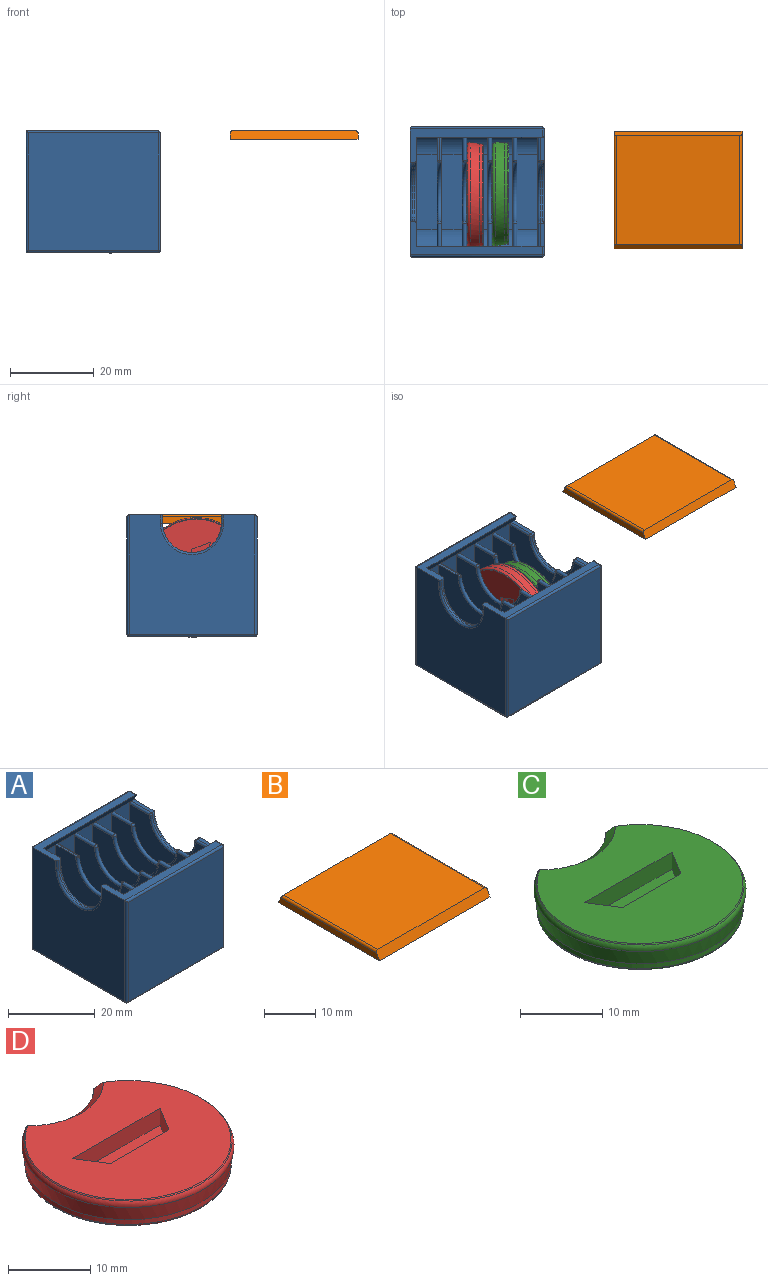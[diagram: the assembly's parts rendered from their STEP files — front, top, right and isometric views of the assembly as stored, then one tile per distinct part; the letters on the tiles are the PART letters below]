
ASSEMBLY  parts=4 mates=3
PART A: 104 faces, bbox 32x31x29 mm
  f0: plane 6.52x0.5mm, normal (0,0,1), area 3.3mm2, adj f13,f52,f53,f59,f84
  f1: plane 6.52x1mm, normal (0,0,1), area 6.5mm2, adj f2,f45,f46,f57,f74
  f2: plane 30x28mm, normal (1,0,0), area 710.8mm2, adj f1,f26,f45,f57,f59,f86,f89,f94
  f3: plane 30x28.5mm, normal (-1,0,0), area 736.6mm2, adj f55,f56,f58,f60,f65,f90,f95,f101
  f4: plane 28x25.5mm, normal (-1,0,0), area 622.4mm2, adj f5,f25,f32,f41,f42,f48,f74,f78
  f5: plane 21x6mm, normal (0,1,0), area 105.1mm2, adj f4,f6,f42,f57,f72,f74
  f6: plane 28x25.5mm, normal (1,0,0), area 622.4mm2, adj f5,f25,f32,f41,f42,f49,f72,f76
  f7: plane 28x25.5mm, normal (-1,0,0), area 622.4mm2, adj f8,f21,f30,f37,f38,f50,f70,f82
  f8: plane 21x6mm, normal (0,1,0), area 105.1mm2, adj f7,f9,f38,f57,f68,f70
  f9: plane 28x25.5mm, normal (1,0,0), area 622.4mm2, adj f8,f21,f30,f37,f38,f51,f68,f80
  f10: plane 28x25.5mm, normal (-1,0,0), area 622.4mm2, adj f11,f22,f29,f35,f36,f51,f68,f80
  f11: plane 21x6mm, normal (0,1,0), area 105.1mm2, adj f10,f12,f36,f57,f66,f68
  f12: plane 28x25.5mm, normal (1,0,0), area 622.4mm2, adj f11,f22,f29,f35,f36,f52,f66,f84
  f13: plane 28x26mm, normal (-1,0,0), area 625.7mm2, adj f0,f14,f23,f28,f33,f34,f52,f66
  f14: plane 21x5.5mm, normal (0,1,0), area 105.1mm2, adj f13,f15,f34,f57,f66
  f15: plane 28x28mm, normal (1,0,0), area 652.9mm2, adj f14,f23,f28,f33,f34,f54,f56,f57
  f16: plane 31x28mm, normal (0,-1,0), area 868mm2, adj f88,f89,f90,f91
  f17: plane 31x28mm, normal (0,1,0), area 868mm2, adj f96,f99,f101,f103
  f18: plane 21x6mm, normal (0,1,0), area 105.1mm2, adj f19,f24,f39,f57,f70,f72
  f19: plane 28x25.5mm, normal (1,0,0), area 622.4mm2, adj f18,f20,f31,f39,f40,f50,f70,f82
  f20: plane 21x6mm, normal (0,-1,0), area 105.1mm2, adj f19,f24,f40,f59,f76,f82
  f21: plane 21x6mm, normal (0,-1,0), area 105.1mm2, adj f7,f9,f37,f59,f80,f82
  f22: plane 21x6mm, normal (0,-1,0), area 105.1mm2, adj f10,f12,f35,f59,f80,f84
  f23: plane 21x5mm, normal (0,-1,0), area 105mm2, adj f13,f15,f33,f59
  f24: plane 28x25.5mm, normal (-1,0,0), area 622.4mm2, adj f18,f20,f31,f39,f40,f49,f72,f76
  f25: plane 21x6mm, normal (0,-1,0), area 105.1mm2, adj f4,f6,f41,f59,f76,f78
  f26: plane 6.52x1mm, normal (0,0,1), area 6.5mm2, adj f2,f45,f47,f59,f78
  f27: plane 31x30mm, normal (0,0,-1), area 930mm2, adj f91,f94,f95,f96
  f28: plane 18x5mm, normal (0,0,1), area 90mm2, adj f13,f15,f33,f34
  f29: plane 18x5mm, normal (0,0,1), area 90mm2, adj f10,f12,f35,f36
  f30: plane 18x5mm, normal (0,0,1), area 90mm2, adj f7,f9,f37,f38
  f31: plane 18x5mm, normal (0,0,1), area 90mm2, adj f19,f24,f39,f40
  f32: plane 18x5mm, normal (0,0,1), area 90mm2, adj f4,f6,f41,f42
  f33: cylinder r=5mm len=5mm, axis (1,0,0), area 39.3mm2, adj f13,f15,f23,f28
  f34: cylinder r=5mm len=5mm, axis (-1,0,0), area 39.3mm2, adj f13,f14,f15,f28
  f35: cylinder r=5mm len=5mm, axis (1,0,0), area 39.3mm2, adj f10,f12,f22,f29
  f36: cylinder r=5mm len=5mm, axis (-1,0,0), area 39.3mm2, adj f10,f11,f12,f29
  f37: cylinder r=5mm len=5mm, axis (1,0,0), area 39.3mm2, adj f7,f9,f21,f30
  f38: cylinder r=5mm len=5mm, axis (-1,0,0), area 39.3mm2, adj f7,f8,f9,f30
  f39: cylinder r=5mm len=5mm, axis (-1,0,0), area 39.3mm2, adj f18,f19,f24,f31
  f40: cylinder r=5mm len=5mm, axis (1,0,0), area 39.3mm2, adj f19,f20,f24,f31
  f41: cylinder r=5mm len=5mm, axis (1,0,0), area 39.3mm2, adj f4,f6,f25,f32
  f42: cylinder r=5mm len=5mm, axis (-1,0,0), area 39.3mm2, adj f4,f5,f6,f32
  f43: cylinder r=7mm len=14mm, axis (-1,0,0), area 11mm2, adj f54,f55,f61,f64
  f44: cylinder r=7mm len=13.97mm, axis (-1,0,0), area 10.5mm2, adj f45,f46,f47,f48
  f45: torus R=7.5mm, axis (1,0,0), area 17.5mm2, adj f1,f2,f26,f44,f46,f47
  f46: cylinder r=0.5mm len=1mm, axis (-1,0,0), area 0.6mm2, adj f1,f44,f45,f75
  f47: cylinder r=0.5mm len=1mm, axis (-1,0,0), area 0.6mm2, adj f26,f44,f45,f79
  f48: torus R=7.5mm, axis (1,0,0), area 17mm2, adj f4,f44,f75,f79
  f49: torus R=7.5mm, axis (1,0,0), area 33.9mm2, adj f6,f24,f73,f77
  f50: torus R=7.5mm, axis (1,0,0), area 33.9mm2, adj f7,f19,f71,f83
  f51: torus R=7.5mm, axis (1,0,0), area 33.9mm2, adj f9,f10,f69,f81
  f52: torus R=7.5mm, axis (1,0,0), area 34.2mm2, adj f0,f12,f13,f53,f67,f85
  f53: cylinder r=0.5mm len=0.5mm, axis (-1,0,0), area 0.2mm2, adj f0,f52,f85
  f54: torus R=7.5mm, axis (1,0,0), area 17.7mm2, adj f15,f43,f62,f63
  f55: torus R=7.5mm, axis (1,0,0), area 17.7mm2, adj f3,f43,f60,f65
  f56: plane 31.5x8mm, normal (0,0,1), area 71.9mm2, adj f3,f15,f57,f63,f64,f65,f86,f88
  f57: plane 30.5x2mm, normal (0,0.89,-0.45), area 68.1mm2, adj f1,f2,f5,f8,f11,f14,f15,f18
  f58: plane 31.5x8mm, normal (0,0,1), area 71.9mm2, adj f3,f15,f59,f60,f61,f62,f100,f103
  f59: plane 30.5x2mm, normal (0,-0.89,-0.45), area 68.1mm2, adj f0,f2,f15,f20,f21,f22,f23,f25
  f60: cylinder r=0.5mm len=2mm, axis (0,0,-1), area 1.6mm2, adj f3,f55,f58,f61
  f61: plane 2x0.5mm, normal (0,-1,0), area 1mm2, adj f43,f58,f60,f62
  f62: cylinder r=0.5mm len=2mm, axis (0,0,-1), area 1.6mm2, adj f15,f54,f58,f61
  f63: cylinder r=0.5mm len=2mm, axis (0,0,-1), area 1.6mm2, adj f15,f54,f56,f64
  f64: plane 2x0.5mm, normal (0,1,0), area 1mm2, adj f43,f56,f63,f65
  f65: cylinder r=0.5mm len=2mm, axis (0,0,-1), area 1.6mm2, adj f3,f55,f56,f64
  f66: cylinder r=0.5mm len=6.52mm, axis (0,-1,0), area 10.2mm2, adj f11,f12,f13,f14,f67
  f67: sphere r=0.5mm, area 0.8mm2, adj f52,f66
  f68: cylinder r=0.5mm len=6.52mm, axis (0,-1,0), area 10.2mm2, adj f8,f9,f10,f11,f69
  f69: sphere r=0.5mm, area 0.8mm2, adj f51,f68
  f70: cylinder r=0.5mm len=6.52mm, axis (0,-1,0), area 10.2mm2, adj f7,f8,f18,f19,f71
  f71: sphere r=0.5mm, area 0.8mm2, adj f50,f70
  f72: cylinder r=0.5mm len=6.52mm, axis (0,-1,0), area 10.2mm2, adj f5,f6,f18,f24,f73
  f73: sphere r=0.5mm, area 0.8mm2, adj f49,f72
  f74: cylinder r=0.5mm len=6.52mm, axis (0,1,0), area 5.1mm2, adj f1,f4,f5,f75
  f75: sphere r=0.5mm, area 0.4mm2, adj f46,f48,f74
  f76: cylinder r=0.5mm len=6.52mm, axis (0,1,0), area 10.2mm2, adj f6,f20,f24,f25,f77
  f77: sphere r=0.5mm, area 0.8mm2, adj f49,f76
  f78: cylinder r=0.5mm len=6.52mm, axis (0,1,0), area 5.1mm2, adj f4,f25,f26,f79
  f79: sphere r=0.5mm, area 0.4mm2, adj f47,f48,f78
  f80: cylinder r=0.5mm len=6.52mm, axis (0,1,0), area 10.2mm2, adj f9,f10,f21,f22,f81
  f81: sphere r=0.5mm, area 0.8mm2, adj f51,f80
  f82: cylinder r=0.5mm len=6.52mm, axis (0,-1,0), area 10.2mm2, adj f7,f19,f20,f21,f83
  f83: sphere r=0.5mm, area 0.8mm2, adj f50,f82
  f84: cylinder r=0.5mm len=6.52mm, axis (0,-1,0), area 5.1mm2, adj f0,f12,f22,f85
  f85: sphere r=0.5mm, area 0.4mm2, adj f52,f53,f84
  f86: cylinder r=0.5mm len=2mm, axis (0,-1,0), area 1.5mm2, adj f2,f56,f57,f87
  f87: sphere r=0.5mm, area 0.4mm2, adj f86,f88,f89
  f88: cylinder r=0.5mm len=31.5mm, axis (-1,0,0), area 24.6mm2, adj f16,f56,f87,f90
  f89: cylinder r=0.5mm len=28mm, axis (0,0,-1), area 22mm2, adj f2,f16,f87,f92
  f90: cylinder r=0.5mm len=28.5mm, axis (0,0,1), area 22.2mm2, adj f3,f16,f88,f93
  f91: cylinder r=0.5mm len=31mm, axis (1,0,0), area 24.3mm2, adj f16,f27,f92,f93
  f92: sphere r=0.5mm, area 0.4mm2, adj f89,f91,f94
  f93: sphere r=0.5mm, area 0.4mm2, adj f90,f91,f95
  f94: cylinder r=0.5mm len=30mm, axis (0,1,0), area 23.6mm2, adj f2,f27,f92,f97
  f95: cylinder r=0.5mm len=30mm, axis (0,-1,0), area 23.6mm2, adj f3,f27,f93,f98
  f96: cylinder r=0.5mm len=31mm, axis (-1,0,0), area 24.3mm2, adj f17,f27,f97,f98
  f97: sphere r=0.5mm, area 0.4mm2, adj f94,f96,f99
  f98: sphere r=0.5mm, area 0.4mm2, adj f95,f96,f101
  f99: cylinder r=0.5mm len=28mm, axis (0,0,1), area 22mm2, adj f2,f17,f97,f102
  f100: cylinder r=0.5mm len=2mm, axis (0,-1,0), area 1.5mm2, adj f2,f58,f59,f102
  f101: cylinder r=0.5mm len=28.5mm, axis (0,0,-1), area 22.2mm2, adj f3,f17,f98,f103
  f102: sphere r=0.5mm, area 0.4mm2, adj f99,f100,f103
  f103: cylinder r=0.5mm len=31.5mm, axis (-1,0,0), area 24.6mm2, adj f17,f58,f101,f102
PART B: 8 faces, bbox 30.5x28x2 mm
  f0: plane 29.5x26mm, normal (0,0,1), area 767mm2, adj f1,f3,f6,f7
  f1: plane 30.5x2mm, normal (0,-0.89,0.45), area 68.1mm2, adj f0,f2,f4,f5,f6,f7
  f2: plane 30.5x28mm, normal (0,0,-1), area 854mm2, adj f1,f3,f4,f5
  f3: plane 30.5x2mm, normal (0,0.89,0.45), area 68.1mm2, adj f0,f2,f4,f5,f6,f7
  f4: plane 28x1.5mm, normal (1,0,0), area 40.9mm2, adj f1,f2,f3,f7
  f5: plane 28x1.5mm, normal (-1,0,0), area 40.9mm2, adj f1,f2,f3,f6
  f6: cylinder r=0.5mm len=26.5mm, axis (0,-1,0), area 20.6mm2, adj f0,f1,f3,f5
  f7: cylinder r=0.5mm len=26.5mm, axis (0,1,0), area 20.6mm2, adj f0,f1,f3,f4
PART C: 29 faces, bbox 27.8x26.4x4 mm
  f0: plane 23.4x22.55mm, normal (0,0,-1), area 356mm2, adj f11,f12,f13,f14,f20,f22
  f1: plane 25x23.19mm, normal (0,0,1), area 401mm2, adj f3,f4,f5,f6,f18,f28
  f2: cone r=13mm half-angle=9.5deg, axis (0,0,1), area 142.3mm2, adj f19,f20,f24,f28
  f3: plane 4x2.5mm, normal (0.85,0.53,0), area 11.8mm2, adj f1,f4,f6,f7
  f4: plane 10x2.5mm, normal (0,1,0), area 25mm2, adj f1,f3,f5,f7
  f5: plane 4x2.5mm, normal (-0.85,0.53,0), area 11.8mm2, adj f1,f4,f6,f7
  f6: plane 15x2.5mm, normal (0,-1,0), area 37.5mm2, adj f1,f3,f5,f7
  f7: plane 15x4mm, normal (0,0,1), area 50mm2, adj f3,f4,f5,f6
  f8: extruded ~3.71x1.54mm, area 4.4mm2, adj f9,f15,f16,f17
  f9: extruded ~3.78x1.54mm, area 4.5mm2, adj f8,f10,f16,f17
  f10: extruded ~3.78x1.56mm, area 4.5mm2, adj f9,f15,f16,f17
  f11: extruded ~5.29x3.49mm, area 7.1mm2, adj f0,f12,f14,f16
  f12: extruded ~5.38x3.49mm, area 7.2mm2, adj f0,f11,f13,f16
  f13: extruded ~5.38x3.47mm, area 7.2mm2, adj f0,f12,f14,f16
  f14: extruded ~5.29x3.47mm, area 7.1mm2, adj f0,f11,f13,f16
  f15: extruded ~3.71x1.56mm, area 4.4mm2, adj f8,f10,f16,f17
  f16: plane 10.67x6.96mm, normal (0,0,-1), area 41.5mm2, adj f8,f9,f10,f11,f12,f13,f14,f15
  f17: plane 7.49x3.1mm, normal (0,0,-1), area 19.4mm2, adj f8,f9,f10,f15
  f18: cone r=12.92mm half-angle=40.3deg, axis (0,0,-1), area 12mm2, adj f1,f19,f28
  f19: torus R=11.86mm, axis (0,0,1), area 58.7mm2, adj f2,f18,f28
  f20: cone r=8.12mm half-angle=9deg, axis (0,0,1), area 24.2mm2, adj f0,f2,f21,f23,f28
  f21: cylinder r=7.65mm len=1mm, axis (0,0,1), area 0.9mm2, adj f20,f22,f24,f25,f26,f27
  f22: cylinder r=11.7mm len=23.4mm, axis (0,0,1), area 45.2mm2, adj f0,f21,f23,f26
  f23: cylinder r=7.65mm len=1mm, axis (0,0,1), area 0.9mm2, adj f20,f22,f24,f25,f26,f27
  f24: cylinder r=12.5mm len=25mm, axis (0,0,1), area 47.6mm2, adj f2,f21,f23,f27
  f25: plane 24.4x23.4mm, normal (0,0,-1), area 13.3mm2, adj f21,f23,f26,f27
  f26: torus R=12mm, axis (0,0,-1), area 30.6mm2, adj f21,f22,f23,f25
  f27: torus R=12.2mm, axis (0,0,-1), area 31.9mm2, adj f21,f23,f24,f25
  f28: cone r=7.97mm half-angle=49.5deg, axis (0,0,1), area 20.8mm2, adj f1,f2,f18,f19,f20
PART D: 44 faces, bbox 27.8x26.4x4 mm
  f0: plane 25x23.19mm, normal (0,0,1), area 401mm2, adj f3,f4,f5,f6,f31,f43
  f1: plane 23.4x22.55mm, normal (0,0,-1), area 386.4mm2, adj f8,f9,f10,f11,f12,f13,f14,f15
  f2: cone r=13mm half-angle=9.5deg, axis (0,0,1), area 142.3mm2, adj f32,f33,f37,f43
  f3: plane 4x2.5mm, normal (0.85,0.53,0), area 11.8mm2, adj f0,f4,f6,f7
  f4: plane 10x2.5mm, normal (0,1,0), area 25mm2, adj f0,f3,f5,f7
  f5: plane 4x2.5mm, normal (-0.85,0.53,0), area 11.8mm2, adj f0,f4,f6,f7
  f6: plane 15x2.5mm, normal (0,-1,0), area 37.5mm2, adj f0,f3,f5,f7
  f7: plane 15x4mm, normal (0,0,1), area 50mm2, adj f3,f4,f5,f6
  f8: plane 1.61x1mm, normal (0,1,0), area 1.6mm2, adj f1,f19,f20,f30
  f9: plane 1.05x1mm, normal (-1,0,0), area 1.1mm2, adj f1,f19,f20,f21
  f10: plane 5.58x1mm, normal (0,-1,0), area 5.6mm2, adj f1,f19,f21,f22
  f11: plane 1.05x1mm, normal (1,0,0), area 1.1mm2, adj f1,f19,f22,f23
  f12: plane 1.33x1mm, normal (0,1,0), area 1.3mm2, adj f1,f19,f23,f24
  f13: plane 8.02x1mm, normal (1,0,0), area 8mm2, adj f1,f19,f24,f25
  f14: plane 1.13x1mm, normal (0,1,0), area 1.1mm2, adj f1,f19,f25,f26
  f15: extruded ~2.08x1mm, area 2.2mm2, adj f1,f19,f26,f27
  f16: plane 1x0.72mm, normal (-1,0,0), area 0.7mm2, adj f1,f19,f27,f28
  f17: plane 1.26x1mm, normal (0,-1,0), area 1.3mm2, adj f1,f19,f28,f29
  f18: plane 5.9x1mm, normal (-1,0,0), area 5.9mm2, adj f1,f19,f29,f30
  f19: plane 10.28x6.18mm, normal (0,0,-1), area 30.5mm2, adj f8,f9,f10,f11,f12,f13,f14,f15
  f20: cylinder r=0.3mm len=1mm, axis (0,0,1), area 0.5mm2, adj f1,f8,f9,f19
  f21: cylinder r=0.3mm len=1mm, axis (0,0,1), area 0.5mm2, adj f1,f9,f10,f19
  f22: cylinder r=0.3mm len=1mm, axis (0,0,1), area 0.5mm2, adj f1,f10,f11,f19
  f23: cylinder r=0.3mm len=1mm, axis (0,0,1), area 0.5mm2, adj f1,f11,f12,f19
  f24: cylinder r=0.3mm len=1mm, axis (0,0,-1), area 0.5mm2, adj f1,f12,f13,f19
  f25: cylinder r=0.3mm len=1mm, axis (0,0,1), area 0.5mm2, adj f1,f13,f14,f19
  f26: cylinder r=0.3mm len=1mm, axis (0,0,1), area 0.2mm2, adj f1,f14,f15,f19
  f27: cylinder r=0.3mm len=1mm, axis (0,0,1), area 0.4mm2, adj f1,f15,f16,f19
  f28: cylinder r=0.3mm len=1mm, axis (0,0,1), area 0.5mm2, adj f1,f16,f17,f19
  f29: cylinder r=0.3mm len=1mm, axis (0,0,-1), area 0.5mm2, adj f1,f17,f18,f19
  f30: cylinder r=0.3mm len=1mm, axis (0,0,-1), area 0.5mm2, adj f1,f8,f18,f19
  f31: cone r=12.92mm half-angle=40.3deg, axis (0,0,-1), area 12mm2, adj f0,f32,f43
  f32: torus R=11.86mm, axis (0,0,1), area 58.7mm2, adj f2,f31,f43
  f33: cone r=8.12mm half-angle=9deg, axis (0,0,1), area 24.2mm2, adj f1,f2,f34,f36,f43
  f34: cylinder r=7.65mm len=0.72mm, axis (0,0,1), area 0.6mm2, adj f33,f35,f37,f39
  f35: cylinder r=11.7mm len=23.4mm, axis (0,0,1), area 45.2mm2, adj f1,f34,f36,f41
  f36: cylinder r=7.65mm len=0.72mm, axis (0,0,1), area 0.6mm2, adj f33,f35,f37,f42
  f37: cylinder r=12.5mm len=25mm, axis (0,0,1), area 47.6mm2, adj f2,f34,f36,f40
  f38: plane 24.4x23.26mm, normal (0,0,-1), area 13.1mm2, adj f39,f40,f41,f42
  f39: torus R=7.95mm, axis (0,0,-1), area 0.3mm2, adj f34,f38,f40,f41
  f40: torus R=12.2mm, axis (0,0,-1), area 31.7mm2, adj f37,f38,f39,f42
  f41: torus R=12mm, axis (0,0,-1), area 30.5mm2, adj f35,f38,f39,f42
  f42: torus R=7.95mm, axis (0,0,-1), area 0.3mm2, adj f36,f38,f40,f41
  f43: cone r=7.97mm half-angle=49.5deg, axis (0,0,1), area 20.8mm2, adj f0,f2,f31,f32,f33
PLACE A at identity
PLACE B t=(47.89,44.41,27)mm
PLACE C rot(axis=(-0.04,-1,0.04),90.1deg) t=(6.5,0,12.68)mm
PLACE D rot(axis=(-0.71,-0.06,0.71),172.6deg) t=(0.5,-1.03,15.49)mm
MATE planar D.f0 <-> A.f9  axis (-1,0,0) through (-2.5,0,15.68)mm
MATE planar C.f2 <-> A.f19  axis (-1,0,0) through (3.5,0,12.68)mm
MATE planar B.f0 <-> A.f58  axis (0,0,1) through (47.89,0.41,29)mm
